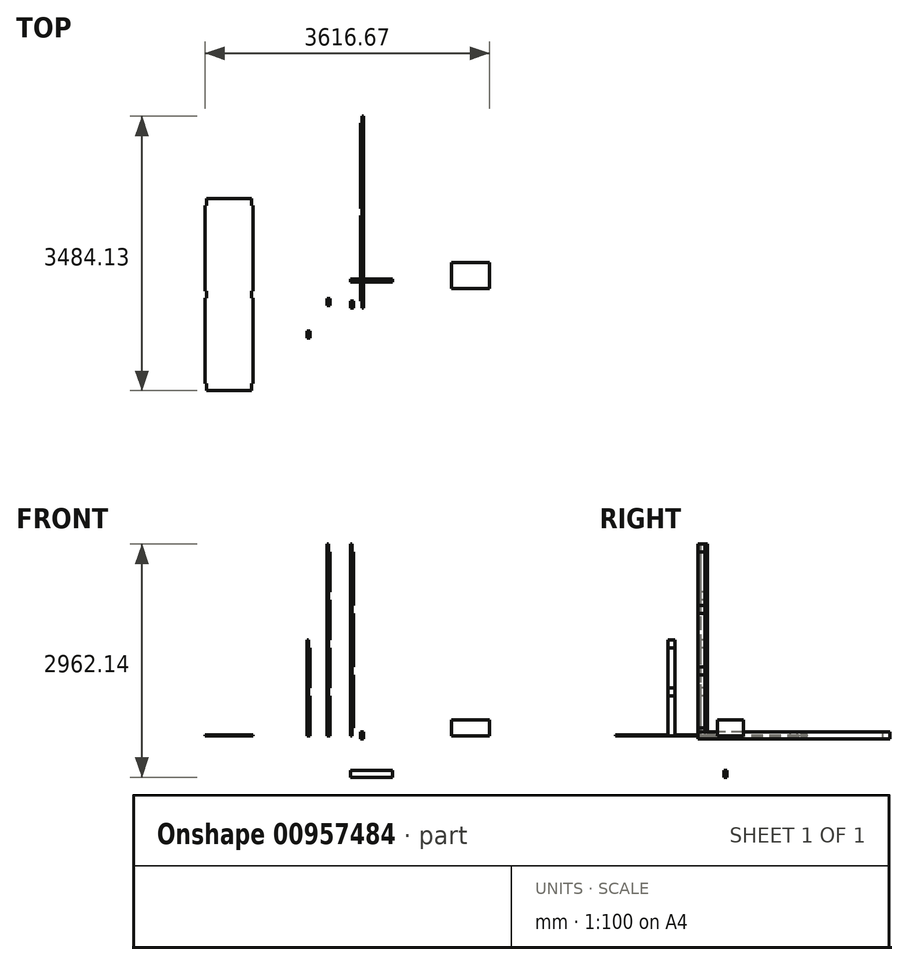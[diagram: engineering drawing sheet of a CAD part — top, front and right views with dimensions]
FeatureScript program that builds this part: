
annotation { "Feature Type Name" : "Feature", "Feature Type Description" : "" }
export const myFeature = defineFeature(function(context is Context, id is Id, definition is map)
    precondition{}
    {
        {
            var Q0;
            Q0=qCreatedBy(makeId("Top.planeOp"),FACE);
            var sketch = newSketch(context, id + "F0", { "sketchPlane" : qUnion([Q0])});
            skLineSegment(sketch, "E0.bottom", {"start": v(0, 0) * mm, "end": v(38.1, 0) * mm});
            skLineSegment(sketch, "E0.top", {"start": v(0, 88.9) * mm, "end": v(38.1, 88.9) * mm});
            skLineSegment(sketch, "E0.left", {"start": v(0, 0) * mm, "end": v(0, 88.9) * mm});
            skLineSegment(sketch, "E0.right", {"start": v(38.1, 0) * mm, "end": v(38.1, 88.9) * mm});
            skSolve(sketch);
        }
        {
            var Q0;
            Q0=makeQuery(id+"F0.imprint","IMPRINT",FACE,{"disambiguationData":[TD([[makeQuery(id+"F0.imprint","IMPRINT",EDGE,{"derivedFrom":sQuery(id+"F0.wireOp",EDGE,"E0.bottom")}),1.0]])]});
            extrude(context, id + "F1", {"entities" : qUnion([Q0]), "depth" : 2438.4 * mm, "offsetDistance" : 25.4 * mm});
        }
        {
            var Q0;
            Q0=qCreatedBy(makeId("Front.planeOp"),FACE);
            var sketch = newSketch(context, id + "F2", { "sketchPlane" : qUnion([Q0])});
            skLineSegment(sketch, "E1.bottom", {"start": v(125.53, 54.67) * mm, "end": v(163.63, 54.67) * mm});
            skLineSegment(sketch, "E1.top", {"start": v(125.53, -34.23) * mm, "end": v(163.63, -34.23) * mm});
            skLineSegment(sketch, "E1.left", {"start": v(125.53, 54.67) * mm, "end": v(125.53, -34.23) * mm});
            skLineSegment(sketch, "E1.right", {"start": v(163.63, 54.67) * mm, "end": v(163.63, -34.23) * mm});
            skSolve(sketch);
        }
        {
            var Q0;
            Q0 = qSketchRegion(id + "F2", true);
            extrude(context, id + "F3", {"entities" : qUnion([Q0]), "oppositeDirection" : true, "depth" : 2438.4 * mm, "offsetDistance" : 25.4 * mm});
        }
        {
            var Q0;
            Q0=qCreatedBy(makeId("Top.planeOp"),FACE);
            var sketch = newSketch(context, id + "F4", { "sketchPlane" : qUnion([Q0])});
            skLineSegment(sketch, "E2.bottom", {"start": v(-1241.45, -1045.73) * mm, "end": v(-1851.05, -1045.73) * mm});
            skLineSegment(sketch, "E2.top", {"start": v(-1241.45, 1392.67) * mm, "end": v(-1851.05, 1392.67) * mm});
            skLineSegment(sketch, "E2.left", {"start": v(-1241.45, -1045.73) * mm, "end": v(-1241.45, 1392.67) * mm});
            skLineSegment(sketch, "E2.right", {"start": v(-1851.05, -1045.73) * mm, "end": v(-1851.05, 1392.67) * mm});
            skSolve(sketch);
        }
        {
            var Q0;
            Q0=makeQuery(id+"F4.imprint","IMPRINT",FACE,{"disambiguationData":[TD([[makeQuery(id+"F4.imprint","IMPRINT",EDGE,{"derivedFrom":sQuery(id+"F4.wireOp",EDGE,"E2.bottom")}),-1.0]])]});
            extrude(context, id + "F5", {"entities" : qUnion([Q0]), "depth" : 12.7 * mm, "offsetDistance" : 25.4 * mm});
        }
        {
            var Q0;
            Q0=qCreatedBy(makeId("Right.planeOp"),FACE);
            var sketch = newSketch(context, id + "F6", { "sketchPlane" : qUnion([Q0])});
            skLineSegment(sketch, "E3.bottom", {"start": v(368.73, -434.84) * mm, "end": v(330.63, -434.84) * mm});
            skLineSegment(sketch, "E3.top", {"start": v(368.73, -523.74) * mm, "end": v(330.63, -523.74) * mm});
            skLineSegment(sketch, "E3.left", {"start": v(368.73, -434.84) * mm, "end": v(368.73, -523.74) * mm});
            skLineSegment(sketch, "E3.right", {"start": v(330.63, -434.84) * mm, "end": v(330.63, -523.74) * mm});
            skSolve(sketch);
        }
        {
            var Q0;
            Q0=makeQuery(id+"F6.imprint","IMPRINT",FACE,{"disambiguationData":[TD([[makeQuery(id+"F6.imprint","IMPRINT",EDGE,{"derivedFrom":sQuery(id+"F6.wireOp",EDGE,"E3.bottom")}),1.0]])]});
            extrude(context, id + "F7", {"entities" : qUnion([Q0]), "depth" : 609.6 * mm - 76.2 * mm, "offsetDistance" : 25.4 * mm});
        }
        {
            var Q0;
            Q0=makeQuery(id+"F3.opExtrude","SWEPT_FACE",FACE,{"disambiguationData":[OSD([sQuery(id+"F2.wireOp",EDGE,"E1.bottom")])]});
            var sketch = newSketch(context, id + "F8", { "sketchPlane" : qUnion([Q0])});
            skLineSegment(sketch, "E4.bottom", {"start": v(125.53, 0) * mm, "end": v(144.58, 0) * mm});
            skLineSegment(sketch, "E4.top", {"start": v(125.53, 88.9) * mm, "end": v(144.58, 88.9) * mm});
            skLineSegment(sketch, "E4.left", {"start": v(125.53, 0) * mm, "end": v(125.53, 88.9) * mm});
            skLineSegment(sketch, "E4.right", {"start": v(144.58, 0) * mm, "end": v(144.58, 88.9) * mm});
            skLineSegment(sketch, "E5.bottom", {"start": v(125.53, 2438.4) * mm, "end": v(144.58, 2438.4) * mm});
            skLineSegment(sketch, "E5.top", {"start": v(125.53, 2349.5) * mm, "end": v(144.58, 2349.5) * mm});
            skLineSegment(sketch, "E5.left", {"start": v(125.53, 2438.4) * mm, "end": v(125.53, 2349.5) * mm});
            skLineSegment(sketch, "E5.right", {"start": v(144.58, 2438.4) * mm, "end": v(144.58, 2349.5) * mm});
            skLineSegment(sketch, "E6.bottom", {"start": v(125.53, 1263.65) * mm, "end": v(144.58, 1263.65) * mm});
            skLineSegment(sketch, "E6.top", {"start": v(125.53, 1174.75) * mm, "end": v(144.58, 1174.75) * mm});
            skLineSegment(sketch, "E6.left", {"start": v(125.53, 1263.65) * mm, "end": v(125.53, 1174.75) * mm});
            skLineSegment(sketch, "E6.right", {"start": v(144.58, 1263.65) * mm, "end": v(144.58, 1174.75) * mm});
            skLineSegment(sketch, "E7.bottom", {"start": v(144.58, 0) * mm, "end": v(163.63, 0) * mm});
            skLineSegment(sketch, "E7.top", {"start": v(144.58, 38.1) * mm, "end": v(163.63, 38.1) * mm});
            skLineSegment(sketch, "E7.left", {"start": v(144.58, 0) * mm, "end": v(144.58, 38.1) * mm});
            skLineSegment(sketch, "E7.right", {"start": v(163.63, 0) * mm, "end": v(163.63, 38.1) * mm});
            skLineSegment(sketch, "E8.bottom", {"start": v(144.58, 1200.15) * mm, "end": v(163.63, 1200.15) * mm});
            skLineSegment(sketch, "E8.top", {"start": v(144.58, 1238.25) * mm, "end": v(163.63, 1238.25) * mm});
            skLineSegment(sketch, "E8.left", {"start": v(144.58, 1200.15) * mm, "end": v(144.58, 1238.25) * mm});
            skLineSegment(sketch, "E8.right", {"start": v(163.63, 1200.15) * mm, "end": v(163.63, 1238.25) * mm});
            skLineSegment(sketch, "E9", {"start": v(163.63, 1219.2) * mm, "end": v(189.83, 1219.2) * mm});
            skLineSegment(sketch, "E10", {"start": v(125.53, 1219.2) * mm, "end": v(114.72, 1219.2) * mm});
            skLineSegment(sketch, "E11.bottom", {"start": v(144.58, 2438.4) * mm, "end": v(163.63, 2438.4) * mm});
            skLineSegment(sketch, "E11.top", {"start": v(144.58, 2400.3) * mm, "end": v(163.63, 2400.3) * mm});
            skLineSegment(sketch, "E11.left", {"start": v(144.58, 2438.4) * mm, "end": v(144.58, 2400.3) * mm});
            skLineSegment(sketch, "E11.right", {"start": v(163.63, 2438.4) * mm, "end": v(163.63, 2400.3) * mm});
            skSolve(sketch);
        }
        {
            var Q0;
            Q0=makeQuery(id+"F8.imprint","IMPRINT",FACE,{"disambiguationData":[TD([[makeQuery(id+"F8.imprint","IMPRINT",EDGE,{"derivedFrom":sQuery(id+"F8.wireOp",EDGE,"E4.bottom")}),1.0]])]});
            var Q1;
            Q1=makeQuery(id+"F8.imprint","IMPRINT",FACE,{"disambiguationData":[TD([[makeQuery(id+"F8.imprint","IMPRINT",EDGE,{"derivedFrom":sQuery(id+"F8.wireOp",EDGE,"E5.bottom")}),-1.0]])]});
            var Q2;
            Q2=makeQuery(id+"F8.imprint","IMPRINT",FACE,{"disambiguationData":[TD([[makeQuery(id+"F8.imprint","IMPRINT",EDGE,{"derivedFrom":sQuery(id+"F8.wireOp",EDGE,"E6.bottom")}),-1.0]])]});
            extrude(context, id + "F9", {"entities" : qUnion([Q0, Q1, Q2]), "operationType" : NewBodyOperationType.REMOVE, "oppositeDirection" : true, "depth" : 88.9 * mm, "offsetDistance" : 25.4 * mm});
        }
        {
            var Q0;
            Q0=makeQuery(id+"F1.opExtrude","SWEPT_FACE",FACE,{"disambiguationData":[OSD([sQuery(id+"F0.wireOp",EDGE,"E0.right")])]});
            var sketch = newSketch(context, id + "F10", { "sketchPlane" : qUnion([Q0])});
            skLineSegment(sketch, "E12.bottom", {"start": v(0, 2438.4) * mm, "end": v(88.9, 2438.4) * mm});
            skLineSegment(sketch, "E12.top", {"start": v(0, 2336.8) * mm, "end": v(88.9, 2336.8) * mm});
            skLineSegment(sketch, "E12.left", {"start": v(0, 2438.4) * mm, "end": v(0, 2336.8) * mm});
            skLineSegment(sketch, "E12.right", {"start": v(88.9, 2438.4) * mm, "end": v(88.9, 2336.8) * mm});
            skLineSegment(sketch, "E13.bottom", {"start": v(0, 0) * mm, "end": v(88.9, 0) * mm});
            skLineSegment(sketch, "E13.top", {"start": v(0, 101.6) * mm, "end": v(88.9, 101.6) * mm});
            skLineSegment(sketch, "E13.left", {"start": v(0, 0) * mm, "end": v(0, 101.6) * mm});
            skLineSegment(sketch, "E13.right", {"start": v(88.9, 0) * mm, "end": v(88.9, 101.6) * mm});
            skLineSegment(sketch, "E14.bottom", {"start": v(88.9, 1659.47) * mm, "end": v(0, 1659.47) * mm});
            skLineSegment(sketch, "E14.top", {"start": v(88.9, 1557.87) * mm, "end": v(0, 1557.87) * mm});
            skLineSegment(sketch, "E14.left", {"start": v(88.9, 1659.47) * mm, "end": v(88.9, 1557.87) * mm});
            skLineSegment(sketch, "E14.right", {"start": v(0, 1659.47) * mm, "end": v(0, 1557.87) * mm});
            skLineSegment(sketch, "E15.bottom", {"start": v(88.9, 880.53) * mm, "end": v(0, 880.53) * mm});
            skLineSegment(sketch, "E15.top", {"start": v(88.9, 778.93) * mm, "end": v(0, 778.93) * mm});
            skLineSegment(sketch, "E15.left", {"start": v(88.9, 880.53) * mm, "end": v(88.9, 778.93) * mm});
            skLineSegment(sketch, "E15.right", {"start": v(0, 880.53) * mm, "end": v(0, 778.93) * mm});
            skSolve(sketch);
        }
        {
            var Q0;
            Q0 = qSketchRegion(id + "F10", true);
            extrude(context, id + "F11", {"entities" : qUnion([Q0]), "operationType" : NewBodyOperationType.REMOVE, "oppositeDirection" : true, "depth" : 19.05 * mm, "offsetDistance" : 25.4 * mm});
        }
        {
            var Q0;
            Q0=makeQuery(id+"F5.opExtrude","CAP_FACE",FACE,{"disambiguationData":[OSD([sQuery(id+"F4.wireOp",EDGE,"E2.bottom"),sQuery(id+"F4.wireOp",EDGE,"E2.top"),sQuery(id+"F4.wireOp",EDGE,"E2.left"),sQuery(id+"F4.wireOp",EDGE,"E2.right")])],"isStart":false});
            var sketch = newSketch(context, id + "F12", { "sketchPlane" : qUnion([Q0])});
            skLineSegment(sketch, "E16.bottom", {"start": v(-1851.05, -1045.73) * mm, "end": v(-1832, -1045.73) * mm});
            skLineSegment(sketch, "E16.top", {"start": v(-1851.05, -956.83) * mm, "end": v(-1832, -956.83) * mm});
            skLineSegment(sketch, "E16.left", {"start": v(-1851.05, -1045.73) * mm, "end": v(-1851.05, -956.83) * mm});
            skLineSegment(sketch, "E16.right", {"start": v(-1832, -1045.73) * mm, "end": v(-1832, -956.83) * mm});
            skLineSegment(sketch, "E17.bottom", {"start": v(-1241.45, -1045.73) * mm, "end": v(-1260.5, -1045.73) * mm});
            skLineSegment(sketch, "E17.top", {"start": v(-1241.45, -956.83) * mm, "end": v(-1260.5, -956.83) * mm});
            skLineSegment(sketch, "E17.left", {"start": v(-1241.45, -1045.73) * mm, "end": v(-1241.45, -956.83) * mm});
            skLineSegment(sketch, "E17.right", {"start": v(-1260.5, -1045.73) * mm, "end": v(-1260.5, -956.83) * mm});
            skLineSegment(sketch, "E18.bottom", {"start": v(-1851.05, 1392.67) * mm, "end": v(-1832, 1392.67) * mm});
            skLineSegment(sketch, "E18.top", {"start": v(-1851.05, 1303.77) * mm, "end": v(-1832, 1303.77) * mm});
            skLineSegment(sketch, "E18.left", {"start": v(-1851.05, 1392.67) * mm, "end": v(-1851.05, 1303.77) * mm});
            skLineSegment(sketch, "E18.right", {"start": v(-1832, 1392.67) * mm, "end": v(-1832, 1303.77) * mm});
            skLineSegment(sketch, "E19.bottom", {"start": v(-1241.45, 1392.67) * mm, "end": v(-1260.5, 1392.67) * mm});
            skLineSegment(sketch, "E19.top", {"start": v(-1241.45, 1303.77) * mm, "end": v(-1260.5, 1303.77) * mm});
            skLineSegment(sketch, "E19.left", {"start": v(-1241.45, 1392.67) * mm, "end": v(-1241.45, 1303.77) * mm});
            skLineSegment(sketch, "E19.right", {"start": v(-1260.5, 1392.67) * mm, "end": v(-1260.5, 1303.77) * mm});
            skLineSegment(sketch, "E20.bottom", {"start": v(-1241.45, 217.92) * mm, "end": v(-1260.5, 217.92) * mm});
            skLineSegment(sketch, "E20.top", {"start": v(-1241.45, 129.02) * mm, "end": v(-1260.5, 129.02) * mm});
            skLineSegment(sketch, "E20.left", {"start": v(-1241.45, 217.92) * mm, "end": v(-1241.45, 129.02) * mm});
            skLineSegment(sketch, "E20.right", {"start": v(-1260.5, 217.92) * mm, "end": v(-1260.5, 129.02) * mm});
            skLineSegment(sketch, "E21", {"start": v(-1851.05, 173.47) * mm, "end": v(-1851.05, 217.92) * mm});
            skLineSegment(sketch, "E22", {"start": v(-1851.05, 217.92) * mm, "end": v(-1832, 217.92) * mm});
            skLineSegment(sketch, "E23", {"start": v(-1832, 217.92) * mm, "end": v(-1832, 129.02) * mm});
            skLineSegment(sketch, "E24", {"start": v(-1832, 129.02) * mm, "end": v(-1851.05, 129.02) * mm});
            skLineSegment(sketch, "E25", {"start": v(-1851.05, 129.02) * mm, "end": v(-1851.05, 173.47) * mm});
            skSolve(sketch);
        }
        {
            var Q0;
            Q0=makeQuery(id+"F12.imprint","IMPRINT",FACE,{"disambiguationData":[TD([[makeQuery(id+"F12.imprint","IMPRINT",EDGE,{"derivedFrom":sQuery(id+"F12.wireOp",EDGE,"E16.bottom")}),-1.0]])]});
            var Q1;
            Q1=makeQuery(id+"F12.imprint","IMPRINT",FACE,{"disambiguationData":[TD([[makeQuery(id+"F12.imprint","IMPRINT",EDGE,{"derivedFrom":sQuery(id+"F12.wireOp",EDGE,"E17.bottom")}),-1.0]])]});
            var Q2;
            Q2=makeQuery(id+"F12.imprint","IMPRINT",FACE,{"disambiguationData":[TD([[makeQuery(id+"F12.imprint","IMPRINT",EDGE,{"derivedFrom":sQuery(id+"F12.wireOp",EDGE,"E20.bottom")}),1.0]])]});
            var Q3;
            Q3=makeQuery(id+"F12.imprint","IMPRINT",FACE,{"disambiguationData":[TD([[makeQuery(id+"F12.imprint","IMPRINT",EDGE,{"derivedFrom":sQuery(id+"F12.wireOp",EDGE,"E21")}),-1.0]])]});
            var Q4;
            Q4=makeQuery(id+"F12.imprint","IMPRINT",FACE,{"disambiguationData":[TD([[makeQuery(id+"F12.imprint","IMPRINT",EDGE,{"derivedFrom":sQuery(id+"F12.wireOp",EDGE,"E18.bottom")}),1.0]])]});
            var Q5;
            Q5=makeQuery(id+"F12.imprint","IMPRINT",FACE,{"disambiguationData":[TD([[makeQuery(id+"F12.imprint","IMPRINT",EDGE,{"derivedFrom":sQuery(id+"F12.wireOp",EDGE,"E19.bottom")}),1.0]])]});
            extrude(context, id + "F13", {"entities" : qUnion([Q0, Q1, Q2, Q3, Q4, Q5]), "operationType" : NewBodyOperationType.REMOVE, "endBound" : BoundingType.UP_TO_NEXT, "oppositeDirection" : true, "depth" : 25.4 * mm, "offsetDistance" : 25.4 * mm});
        }
        {
            var Q0;
            Q0=qCreatedBy(makeId("Top.planeOp"),FACE);
            var sketch = newSketch(context, id + "F14", { "sketchPlane" : qUnion([Q0])});
            skLineSegment(sketch, "E26.bottom", {"start": v(1283.02, 579.35) * mm, "end": v(1765.62, 579.35) * mm});
            skLineSegment(sketch, "E26.top", {"start": v(1283.02, 249.15) * mm, "end": v(1765.62, 249.15) * mm});
            skLineSegment(sketch, "E26.left", {"start": v(1283.02, 579.35) * mm, "end": v(1283.02, 249.15) * mm});
            skLineSegment(sketch, "E26.right", {"start": v(1765.62, 579.35) * mm, "end": v(1765.62, 249.15) * mm});
            skSolve(sketch);
        }
        {
            var Q0;
            Q0=makeQuery(id+"F14.imprint","IMPRINT",FACE,{"disambiguationData":[TD([[makeQuery(id+"F14.imprint","IMPRINT",EDGE,{"derivedFrom":sQuery(id+"F14.wireOp",EDGE,"E26.bottom")}),-1.0]])]});
            extrude(context, id + "F15", {"entities" : qUnion([Q0]), "depth" : 203.2 * mm, "offsetDistance" : 25.4 * mm});
        }
        {
            var Q0;
            Q0=qCreatedBy(makeId("Top.planeOp"),FACE);
            var sketch = newSketch(context, id + "F16", { "sketchPlane" : qUnion([Q0])});
            skLineSegment(sketch, "E27.bottom", {"start": v(-296.84, 35.1) * mm, "end": v(-258.74, 35.1) * mm});
            skLineSegment(sketch, "E27.top", {"start": v(-296.84, 124) * mm, "end": v(-258.74, 124) * mm});
            skLineSegment(sketch, "E27.left", {"start": v(-296.84, 35.1) * mm, "end": v(-296.84, 124) * mm});
            skLineSegment(sketch, "E27.right", {"start": v(-258.74, 35.1) * mm, "end": v(-258.74, 124) * mm});
            skSolve(sketch);
        }
        {
            var Q0;
            Q0=makeQuery(id+"F16.imprint","IMPRINT",FACE,{"disambiguationData":[TD([[makeQuery(id+"F16.imprint","IMPRINT",EDGE,{"derivedFrom":sQuery(id+"F16.wireOp",EDGE,"E27.bottom")}),1.0]])]});
            extrude(context, id + "F17", {"entities" : qUnion([Q0]), "depth" : 2438.4 * mm, "offsetDistance" : 25.4 * mm});
        }
        {
            var Q0;
            Q0=makeQuery(id+"F17.opExtrude","SWEPT_FACE",FACE,{"disambiguationData":[OSD([sQuery(id+"F16.wireOp",EDGE,"E27.bottom")])]});
            var sketch = newSketch(context, id + "F18", { "sketchPlane" : qUnion([Q0])});
            skLineSegment(sketch, "E28.bottom", {"start": v(-258.74, 2438.4) * mm, "end": v(-277.79, 2438.4) * mm});
            skLineSegment(sketch, "E28.top", {"start": v(-258.74, 2336.8) * mm, "end": v(-277.79, 2336.8) * mm});
            skLineSegment(sketch, "E28.left", {"start": v(-258.74, 2438.4) * mm, "end": v(-258.74, 2336.8) * mm});
            skLineSegment(sketch, "E28.right", {"start": v(-277.79, 2438.4) * mm, "end": v(-277.79, 2336.8) * mm});
            skLineSegment(sketch, "E29.0.1.0", {"start": v(-258.74, 1828.8) * mm, "end": v(-258.74, 1727.2) * mm});
            skLineSegment(sketch, "E29.0.1.1", {"start": v(-277.79, 1828.8) * mm, "end": v(-277.79, 1727.2) * mm});
            skLineSegment(sketch, "E29.0.1.2", {"start": v(-258.74, 1727.2) * mm, "end": v(-277.79, 1727.2) * mm});
            skLineSegment(sketch, "E29.0.1.3", {"start": v(-258.74, 1828.8) * mm, "end": v(-277.79, 1828.8) * mm});
            skLineSegment(sketch, "E29.0.2.0", {"start": v(-258.74, 1219.2) * mm, "end": v(-258.74, 1117.6) * mm});
            skLineSegment(sketch, "E29.0.2.1", {"start": v(-277.79, 1219.2) * mm, "end": v(-277.79, 1117.6) * mm});
            skLineSegment(sketch, "E29.0.2.2", {"start": v(-258.74, 1117.6) * mm, "end": v(-277.79, 1117.6) * mm});
            skLineSegment(sketch, "E29.0.2.3", {"start": v(-258.74, 1219.2) * mm, "end": v(-277.79, 1219.2) * mm});
            skLineSegment(sketch, "E29.0.3.0", {"start": v(-258.74, 609.6) * mm, "end": v(-258.74, 508) * mm});
            skLineSegment(sketch, "E29.0.3.1", {"start": v(-277.79, 609.6) * mm, "end": v(-277.79, 508) * mm});
            skLineSegment(sketch, "E29.0.3.2", {"start": v(-258.74, 508) * mm, "end": v(-277.79, 508) * mm});
            skLineSegment(sketch, "E29.0.3.3", {"start": v(-258.74, 609.6) * mm, "end": v(-277.79, 609.6) * mm});
            skLineSegment(sketch, "E29.direction1", {"start": v(-258.74, 2336.8) * mm, "end": v(-233.34, 2336.8) * mm, "construction": true});
            skLineSegment(sketch, "E29.direction2", {"start": v(-258.74, 2336.8) * mm, "end": v(-258.74, 1727.2) * mm, "construction": true});
            skSolve(sketch);
        }
        {
            var Q0;
            Q0=makeQuery(id+"F18.imprint","IMPRINT",FACE,{"disambiguationData":[TD([[makeQuery(id+"F18.imprint","IMPRINT",EDGE,{"derivedFrom":sQuery(id+"F18.wireOp",EDGE,"E28.bottom")}),-1.0]])]});
            var Q1;
            Q1=makeQuery(id+"F18.imprint","IMPRINT",FACE,{"disambiguationData":[TD([[makeQuery(id+"F18.imprint","IMPRINT",EDGE,{"derivedFrom":sQuery(id+"F18.wireOp",EDGE,"E29.0.1.0")}),-1.0]])]});
            var Q2;
            Q2=makeQuery(id+"F18.imprint","IMPRINT",FACE,{"disambiguationData":[TD([[makeQuery(id+"F18.imprint","IMPRINT",EDGE,{"derivedFrom":sQuery(id+"F18.wireOp",EDGE,"E29.0.2.0")}),-1.0]])]});
            var Q3;
            Q3=makeQuery(id+"F18.imprint","IMPRINT",FACE,{"disambiguationData":[TD([[makeQuery(id+"F18.imprint","IMPRINT",EDGE,{"derivedFrom":sQuery(id+"F18.wireOp",EDGE,"E29.0.3.0")}),-1.0]])]});
            extrude(context, id + "F19", {"entities" : qUnion([Q0, Q1, Q2, Q3]), "operationType" : NewBodyOperationType.REMOVE, "endBound" : BoundingType.UP_TO_NEXT, "oppositeDirection" : true, "depth" : 25.4 * mm, "offsetDistance" : 25.4 * mm});
        }
        {
            var Q0;
            Q0=qCreatedBy(makeId("Top.planeOp"),FACE);
            var sketch = newSketch(context, id + "F20", { "sketchPlane" : qUnion([Q0])});
            skLineSegment(sketch, "E30.bottom", {"start": v(-554.07, -378.28) * mm, "end": v(-515.97, -378.28) * mm});
            skLineSegment(sketch, "E30.top", {"start": v(-554.07, -289.38) * mm, "end": v(-515.97, -289.38) * mm});
            skLineSegment(sketch, "E30.left", {"start": v(-554.07, -378.28) * mm, "end": v(-554.07, -289.38) * mm});
            skLineSegment(sketch, "E30.right", {"start": v(-515.97, -378.28) * mm, "end": v(-515.97, -289.38) * mm});
            skSolve(sketch);
        }
        {
            var Q0;
            Q0=makeQuery(id+"F20.imprint","IMPRINT",FACE,{"disambiguationData":[TD([[makeQuery(id+"F20.imprint","IMPRINT",EDGE,{"derivedFrom":sQuery(id+"F20.wireOp",EDGE,"E30.bottom")}),1.0]])]});
            extrude(context, id + "F21", {"entities" : qUnion([Q0]), "depth" : 1219.2 * mm, "offsetDistance" : 25.4 * mm});
        }
        {
            var Q0;
            Q0=makeQuery(id+"F21.opExtrude","SWEPT_FACE",FACE,{"disambiguationData":[OSD([sQuery(id+"F20.wireOp",EDGE,"E30.bottom")])]});
            var sketch = newSketch(context, id + "F22", { "sketchPlane" : qUnion([Q0])});
            skLineSegment(sketch, "E31.bottom", {"start": v(-515.97, 1219.2) * mm, "end": v(-535.02, 1219.2) * mm});
            skLineSegment(sketch, "E31.top", {"start": v(-515.97, 1117.6) * mm, "end": v(-535.02, 1117.6) * mm});
            skLineSegment(sketch, "E31.left", {"start": v(-515.97, 1219.2) * mm, "end": v(-515.97, 1117.6) * mm});
            skLineSegment(sketch, "E31.right", {"start": v(-535.02, 1219.2) * mm, "end": v(-535.02, 1117.6) * mm});
            skLineSegment(sketch, "E32.0.1.0", {"start": v(-535.02, 609.6) * mm, "end": v(-535.02, 508) * mm});
            skLineSegment(sketch, "E32.0.1.1", {"start": v(-515.97, 609.6) * mm, "end": v(-535.02, 609.6) * mm});
            skLineSegment(sketch, "E32.0.1.2", {"start": v(-515.97, 609.6) * mm, "end": v(-515.97, 508) * mm});
            skLineSegment(sketch, "E32.0.1.3", {"start": v(-515.97, 508) * mm, "end": v(-535.02, 508) * mm});
            skLineSegment(sketch, "E32.direction1", {"start": v(-535.02, 1117.6) * mm, "end": v(-509.62, 1117.6) * mm, "construction": true});
            skLineSegment(sketch, "E32.direction2", {"start": v(-535.02, 1117.6) * mm, "end": v(-535.02, 508) * mm, "construction": true});
            skSolve(sketch);
        }
        {
            var Q0;
            Q0=makeQuery(id+"F22.imprint","IMPRINT",FACE,{"disambiguationData":[TD([[makeQuery(id+"F22.imprint","IMPRINT",EDGE,{"derivedFrom":sQuery(id+"F22.wireOp",EDGE,"E31.bottom")}),-1.0]])]});
            var Q1;
            Q1=makeQuery(id+"F22.imprint","IMPRINT",FACE,{"disambiguationData":[TD([[makeQuery(id+"F22.imprint","IMPRINT",EDGE,{"derivedFrom":sQuery(id+"F22.wireOp",EDGE,"E32.0.1.0")}),1.0]])]});
            extrude(context, id + "F23", {"entities" : qUnion([Q0, Q1]), "operationType" : NewBodyOperationType.REMOVE, "endBound" : BoundingType.UP_TO_NEXT, "oppositeDirection" : true, "depth" : 25.4 * mm, "offsetDistance" : 25.4 * mm});
        }
    });
